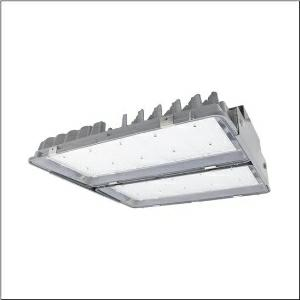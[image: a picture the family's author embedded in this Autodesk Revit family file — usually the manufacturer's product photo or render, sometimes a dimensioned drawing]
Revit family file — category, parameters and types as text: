
# Revit family: highbay_11xtreme_51hf61db4qma
name_source: partatom
category: Lighting Fixtures
units: mm (PartAtom-declared; Revit-internal decimal feet)

## family parameters
Cut with Voids When Loaded = No
Host = Face
Light Source = No
Part Type = Normal
Room Calculation Point = No
Round Connector Dimension = Use Diameter
Shared = No

## types (1)
- --- (1 x LED, 37300 lm, 193.8 W, 4000K)
    Apparent Load = 194 VA
    CIE Flux Codes = 88 96 99 100 100
    Color Rendering = 80
    Color Temperature = 4000K
    Default Elevation = 1800 mm
    Description = Highbay 11Xtreme, high bay luminaire, primary light control with lens, of PMMA, primary optical cover: cover, of toughened safety glass, light emission: direct distribution, primary light characteristic: symmetric, installation type: suspended mounting, surface-mounted, 2x LED module,for 1x 2x LED, rated luminous flux: 36.000lm, luminous efficacy: 178lm/W, light colour: 840, colour temperature: 4000K, control gear: DALI 2 (with two DALI addresses), with cable H07RN-F 5x 1.5mm², mains connection: 220..240V, AC, 50/60Hz, cable length: 1,5m, rated input power: 202W, luminaire housing, of diecast aluminium, coated, silver, length: 595mm, width: 560mm, height: 195mm, protection rating (complete): IP66, insulation class (complete): insulation class I (protective earthing), certification: CE, ENEC, UKCA, protection symbol: D, ball protection: ball impact resistant according to DIN VDE 0710 part 13 (with chain suspension), impact resistance: IK08, permissible operating ambient temperature: -25..+70°C, reducing of maximum allowable ambient temperature of 5°C with ceiling mounting, packaging unit: 1 piece
    Height = 157 mm
    Lamp = 1 x LED
    Lamp Light Flux = 37300 lm
    Lamp Power = 193.8 W
    Lamp count = 1
    Length = 593 mm
    Luminous efficacy = 192 lm/W
    Manufacturer = Siteco
    ModVariant = No
    Model = 51HF61DB4QMA
    Mounting Place = Ceiling
    Mounting Type = Pendant
    Number of Poles = 1
    OnlyDefault = Yes
    Power Factor = 1
    Product Name = Highbay 11Xtreme
    Product group = high bay luminaire
    ProductGroupID = 901
    Protection Class = Protection class I
    Protection Degree = IP 66
    RLX_Detail_Level = 1
    RLX_Emergency_Light_Flux = 0 lm
    RLX_Emergency_Type = 0
    RLX_Emergency_Type_DB = No
    RlxData = <blob elided: 33789 chars, md5=d9e5c979>
    Socket = socket
    Standby Power = 0 W
    System Light Flux = 37301 lm
    System Power = 194 W
    Type Comments = factory setting: luminous flux: 100 % | dim-lin: 254 | 648 mA
    Type Image = l_1258340.jpg
    URL = http://relux.com
    VarID = @adj_083530
    Voltage = 0 V
    Weight = 0.00 kg
    Width = 278 mm

## geometry (parser evidence)
native form markers: Blend x4, Sweep x10
no freeform markers — native parametric forms only
